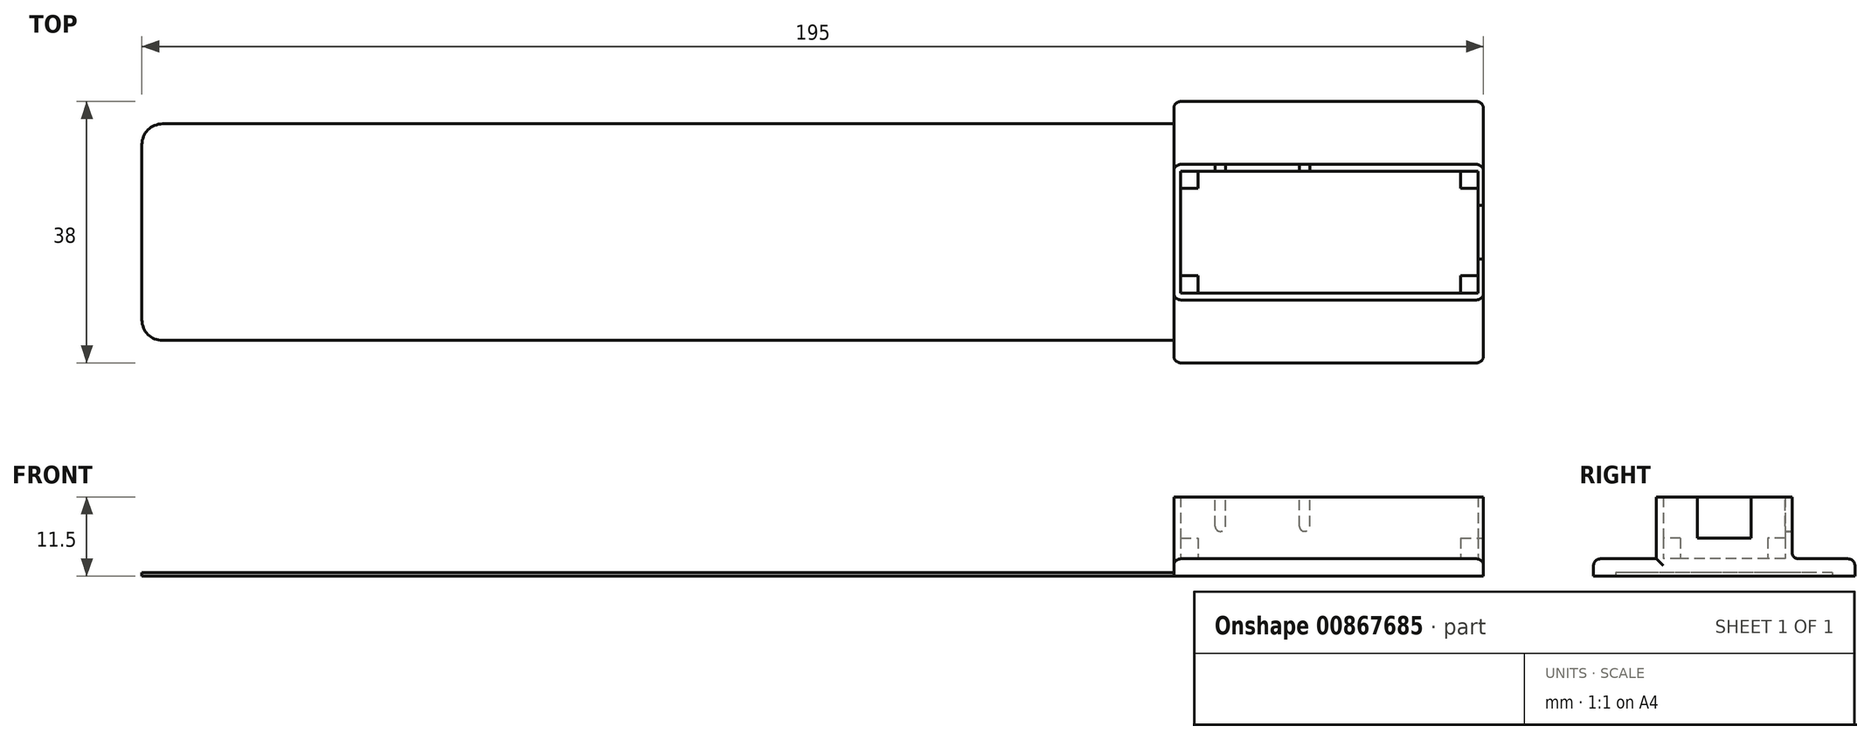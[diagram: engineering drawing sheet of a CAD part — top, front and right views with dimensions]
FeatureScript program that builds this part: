
annotation { "Feature Type Name" : "Feature", "Feature Type Description" : "" }
export const myFeature = defineFeature(function(context is Context, id is Id, definition is map)
    precondition{}
    {
        {
            var Q0;
            Q0=qCreatedBy(makeId("Top.planeOp"),FACE);
            var sketch = newSketch(context, id + "F0", { "sketchPlane" : qUnion([Q0])});
            skLineSegment(sketch, "E0.bottom", {"start": v(0, 19) * mm, "end": v(45, 19) * mm});
            skLineSegment(sketch, "E0.top", {"start": v(0, -19) * mm, "end": v(45, -19) * mm});
            skLineSegment(sketch, "E0.left", {"start": v(0, 19) * mm, "end": v(0, -19) * mm});
            skLineSegment(sketch, "E0.right", {"start": v(45, 19) * mm, "end": v(45, -19) * mm});
            skLineSegment(sketch, "E1.bottom", {"start": v(0, 15.75) * mm, "end": v(-147, 15.75) * mm});
            skLineSegment(sketch, "E1.top", {"start": v(0, -15.75) * mm, "end": v(-147, -15.75) * mm});
            skLineSegment(sketch, "E1.left", {"start": v(0, 15.75) * mm, "end": v(0, -15.75) * mm});
            skLineSegment(sketch, "E1.right", {"start": v(-150, 12.75) * mm, "end": v(-150, -12.75) * mm});
            skPoint(sketch, "E2.visualSharp", {"position": v(-150, 15.75) * mm});
            skArc(sketch, "E2.filletArc", {"start": v(-147, 15.75) * mm, "mid": v(-149.12, 14.87) * mm, "end": v(-150, 12.75) * mm});
            skPoint(sketch, "E3.visualSharp", {"position": v(-150, -15.75) * mm});
            skArc(sketch, "E3.filletArc", {"start": v(-150, -12.75) * mm, "mid": v(-149.12, -14.87) * mm, "end": v(-147, -15.75) * mm});
            skSolve(sketch);
        }
        {
            var Q0;
            Q0=makeQuery(id+"F0.imprint","IMPRINT",FACE,{"disambiguationData":[TD([[makeQuery(id+"F0.imprint","IMPRINT",EDGE,{"derivedFrom":sQuery(id+"F0.wireOp",EDGE,"E1.bottom")}),1.0]])]});
            var Q1;
            {var subQ3=sQuery(id+"F0.wireOp",EDGE,"E0.bottom");Q1=makeQuery(id+"F0.imprint","IMPRINT",FACE,{"disambiguationData":[TD([[makeQuery(id+"F0.imprint","IMPRINT",EDGE,{"derivedFrom":subQ3}),-1.0]])]});}
            extrude(context, id + "F1", {"entities" : qUnion([Q0, Q1]), "depth" : .5 * mm, "offsetDistance" : 25 * mm});
        }
        {
            var Q0;
            Q0=makeQuery(id+"F1.opExtrude","CAP_FACE",FACE,{"disambiguationData":[OSD([sQuery(id+"F0.wireOp",EDGE,"E0.bottom"),sQuery(id+"F0.wireOp",EDGE,"E0.top"),sQuery(id+"F0.wireOp",EDGE,"E0.left"),sQuery(id+"F0.wireOp",EDGE,"E0.right"),sQuery(id+"F0.wireOp",EDGE,"E1.bottom"),sQuery(id+"F0.wireOp",EDGE,"E1.top"),sQuery(id+"F0.wireOp",EDGE,"E1.right"),sQuery(id+"F0.wireOp",EDGE,"E2.filletArc"),sQuery(id+"F0.wireOp",EDGE,"E3.filletArc")])],"isStart":false});
            var sketch = newSketch(context, id + "F2", { "sketchPlane" : qUnion([Q0])});
            skLineSegment(sketch, "E4.bottom", {"start": v(45, 19) * mm, "end": v(0, 19) * mm});
            skLineSegment(sketch, "E4.top", {"start": v(45, -19) * mm, "end": v(0, -19) * mm});
            skLineSegment(sketch, "E4.left", {"start": v(45, 19) * mm, "end": v(45, -19) * mm});
            skLineSegment(sketch, "E4.right", {"start": v(0, 19) * mm, "end": v(0, -19) * mm});
            skSolve(sketch);
        }
        {
            var Q0;
            {var subQ1=sQuery(id+"F2.wireOp",EDGE,"E4.bottom");Q0=makeQuery(id+"F2.imprint","IMPRINT",FACE,{"disambiguationData":[TD([[makeQuery(id+"F2.imprint","IMPRINT",EDGE,{"derivedFrom":subQ1}),-1.0]])]});}
            extrude(context, id + "F3", {"entities" : qUnion([Q0]), "operationType" : NewBodyOperationType.ADD, "depth" : 2 * mm, "offsetDistance" : 25 * mm});
        }
        {
            var Q0;
            Q0=makeQuery(id+"F3.opExtrude","CAP_FACE",FACE,{"disambiguationData":[OSD([sQuery(id+"F2.wireOp",EDGE,"E4.bottom"),sQuery(id+"F2.wireOp",EDGE,"E4.top"),sQuery(id+"F2.wireOp",EDGE,"E4.left"),sQuery(id+"F2.wireOp",EDGE,"E4.right")])],"isStart":false});
            var sketch = newSketch(context, id + "F4", { "sketchPlane" : qUnion([Q0])});
            skLineSegment(sketch, "E5.bottom", {"start": v(1, 8.85) * mm, "end": v(44.2, 8.85) * mm});
            skLineSegment(sketch, "E5.top", {"start": v(1, -8.85) * mm, "end": v(44.2, -8.85) * mm});
            skLineSegment(sketch, "E5.left", {"start": v(1, 8.85) * mm, "end": v(1, -8.85) * mm});
            skLineSegment(sketch, "E5.right", {"start": v(44.2, 8.85) * mm, "end": v(44.2, -8.85) * mm});
            skLineSegment(sketch, "E6.bottom", {"start": v(0, 9.85) * mm, "end": v(45, 9.85) * mm});
            skLineSegment(sketch, "E6.top", {"start": v(0, -9.85) * mm, "end": v(45, -9.85) * mm});
            skLineSegment(sketch, "E6.left", {"start": v(0, 9.85) * mm, "end": v(0, -9.85) * mm});
            skLineSegment(sketch, "E6.right", {"start": v(45, 9.85) * mm, "end": v(45, -9.85) * mm});
            skSolve(sketch);
        }
        {
            var Q0;
            Q0=makeQuery(id+"F4.imprint","IMPRINT",FACE,{"disambiguationData":[TD([[makeQuery(id+"F4.imprint","IMPRINT",EDGE,{"derivedFrom":sQuery(id+"F4.wireOp",EDGE,"E5.bottom")}),1.0]])]});
            extrude(context, id + "F5", {"entities" : qUnion([Q0]), "operationType" : NewBodyOperationType.ADD, "depth" : 9 * mm, "offsetDistance" : 25 * mm});
        }
        {
            var Q0;
            Q0=makeQuery(id+"F5.boolean.opBoolean","SPLIT",FACE,{"disambiguationData":[TD([makeQuery(id+"F5.opExtrude","SWEPT_FACE",FACE,{"disambiguationData":[OSD([sQuery(id+"F4.wireOp",EDGE,"E5.bottom")])]})])],"derivedFrom":makeQuery(id+"F3.opExtrude","CAP_FACE",FACE,{"disambiguationData":[OSD([sQuery(id+"F2.wireOp",EDGE,"E4.bottom"),sQuery(id+"F2.wireOp",EDGE,"E4.top"),sQuery(id+"F2.wireOp",EDGE,"E4.left"),sQuery(id+"F2.wireOp",EDGE,"E4.right")])],"isStart":false})});
            var sketch = newSketch(context, id + "F6", { "sketchPlane" : qUnion([Q0])});
            skLineSegment(sketch, "E7.bottom", {"start": v(1, 6.35) * mm, "end": v(3.5, 6.35) * mm});
            skLineSegment(sketch, "E7.top", {"start": v(1, 8.85) * mm, "end": v(3.5, 8.85) * mm});
            skLineSegment(sketch, "E7.left", {"start": v(1, 6.35) * mm, "end": v(1, 8.85) * mm});
            skLineSegment(sketch, "E7.right", {"start": v(3.5, 6.35) * mm, "end": v(3.5, 8.85) * mm});
            skLineSegment(sketch, "E8.bottom", {"start": v(1, -6.35) * mm, "end": v(3.5, -6.35) * mm});
            skLineSegment(sketch, "E8.top", {"start": v(1, -8.85) * mm, "end": v(3.5, -8.85) * mm});
            skLineSegment(sketch, "E8.left", {"start": v(1, -6.35) * mm, "end": v(1, -8.85) * mm});
            skLineSegment(sketch, "E8.right", {"start": v(3.5, -6.35) * mm, "end": v(3.5, -8.85) * mm});
            skLineSegment(sketch, "E9.bottom", {"start": v(41.7, -8.85) * mm, "end": v(44.2, -8.85) * mm});
            skLineSegment(sketch, "E9.top", {"start": v(41.7, -6.35) * mm, "end": v(44.2, -6.35) * mm});
            skLineSegment(sketch, "E9.left", {"start": v(41.7, -8.85) * mm, "end": v(41.7, -6.35) * mm});
            skLineSegment(sketch, "E9.right", {"start": v(44.2, -8.85) * mm, "end": v(44.2, -6.35) * mm});
            skLineSegment(sketch, "E10.bottom", {"start": v(41.7, 8.85) * mm, "end": v(44.2, 8.85) * mm});
            skLineSegment(sketch, "E10.top", {"start": v(41.7, 6.35) * mm, "end": v(44.2, 6.35) * mm});
            skLineSegment(sketch, "E10.left", {"start": v(41.7, 8.85) * mm, "end": v(41.7, 6.35) * mm});
            skLineSegment(sketch, "E10.right", {"start": v(44.2, 8.85) * mm, "end": v(44.2, 6.35) * mm});
            skSolve(sketch);
        }
        {
            var Q0;
            Q0=makeQuery(id+"F6.imprint","IMPRINT",FACE,{"disambiguationData":[TD([[makeQuery(id+"F6.imprint","IMPRINT",EDGE,{"derivedFrom":sQuery(id+"F6.wireOp",EDGE,"E7.bottom")}),1.0]])]});
            var Q1;
            Q1=makeQuery(id+"F6.imprint","IMPRINT",FACE,{"disambiguationData":[TD([[makeQuery(id+"F6.imprint","IMPRINT",EDGE,{"derivedFrom":sQuery(id+"F6.wireOp",EDGE,"E10.bottom")}),-1.0]])]});
            var Q2;
            Q2=makeQuery(id+"F6.imprint","IMPRINT",FACE,{"disambiguationData":[TD([[makeQuery(id+"F6.imprint","IMPRINT",EDGE,{"derivedFrom":sQuery(id+"F6.wireOp",EDGE,"E9.bottom")}),1.0]])]});
            var Q3;
            Q3=makeQuery(id+"F6.imprint","IMPRINT",FACE,{"disambiguationData":[TD([[makeQuery(id+"F6.imprint","IMPRINT",EDGE,{"derivedFrom":sQuery(id+"F6.wireOp",EDGE,"E8.bottom")}),-1.0]])]});
            extrude(context, id + "F7", {"entities" : qUnion([Q0, Q1, Q2, Q3]), "operationType" : NewBodyOperationType.ADD, "depth" : 3 * mm, "offsetDistance" : 25 * mm});
        }
        {
            var Q0;
            Q0=makeQuery(id+"F5.boolean.opBoolean","MERGE",FACE,{"derivedFrom":[makeQuery(id+"F3.boolean.opBoolean","MERGE",FACE,{"derivedFrom":[makeQuery(id+"F1.opExtrude","SWEPT_FACE",FACE,{"disambiguationData":[OSD([sQuery(id+"F0.wireOp",EDGE,"E0.right")])]}),makeQuery(id+"F3.opExtrude","SWEPT_FACE",FACE,{"disambiguationData":[OSD([sQuery(id+"F2.wireOp",EDGE,"E4.left")])]})]}),makeQuery(id+"F5.opExtrude","SWEPT_FACE",FACE,{"disambiguationData":[OSD([sQuery(id+"F4.wireOp",EDGE,"E6.right")])]})]});
            var sketch = newSketch(context, id + "F8", { "sketchPlane" : qUnion([Q0])});
            skLineSegment(sketch, "E11.bottom", {"start": v(-3.9, 11.5) * mm, "end": v(3.9, 11.5) * mm});
            skLineSegment(sketch, "E11.top", {"start": v(-3.9, 5.5) * mm, "end": v(3.9, 5.5) * mm});
            skLineSegment(sketch, "E11.left", {"start": v(-3.9, 11.5) * mm, "end": v(-3.9, 5.5) * mm});
            skLineSegment(sketch, "E11.right", {"start": v(3.9, 11.5) * mm, "end": v(3.9, 5.5) * mm});
            skSolve(sketch);
        }
        {
            var Q0;
            Q0=makeQuery(id+"F8.imprint","IMPRINT",FACE,{"disambiguationData":[TD([[makeQuery(id+"F8.imprint","IMPRINT",EDGE,{"derivedFrom":sQuery(id+"F8.wireOp",EDGE,"E11.bottom")}),1.0]])]});
            extrude(context, id + "F9", {"entities" : qUnion([Q0]), "operationType" : NewBodyOperationType.REMOVE, "endBound" : BoundingType.UP_TO_NEXT, "oppositeDirection" : true, "depth" : 25 * mm, "offsetDistance" : 25 * mm});
        }
        {
            var Q0;
            Q0=makeQuery(id+"F5.opExtrude","SWEPT_FACE",FACE,{"disambiguationData":[OSD([sQuery(id+"F4.wireOp",EDGE,"E6.bottom")])]});
            var sketch = newSketch(context, id + "F10", { "sketchPlane" : qUnion([Q0])});
            skLineSegment(sketch, "E12.bottom", {"start": v(-19.75, 11.5) * mm, "end": v(-18.25, 11.5) * mm});
            skLineSegment(sketch, "E12.top", {"start": v(-19.75, 6.5) * mm, "end": v(-18.25, 6.5) * mm});
            skLineSegment(sketch, "E12.left", {"start": v(-19.75, 11.5) * mm, "end": v(-19.75, 6.5) * mm});
            skLineSegment(sketch, "E12.right", {"start": v(-18.25, 11.5) * mm, "end": v(-18.25, 6.5) * mm});
            skLineSegment(sketch, "E13.bottom", {"start": v(-7.5, 11.5) * mm, "end": v(-6, 11.5) * mm});
            skLineSegment(sketch, "E13.top", {"start": v(-7.5, 6.5) * mm, "end": v(-6, 6.5) * mm});
            skLineSegment(sketch, "E13.left", {"start": v(-7.5, 11.5) * mm, "end": v(-7.5, 6.5) * mm});
            skLineSegment(sketch, "E13.right", {"start": v(-6, 11.5) * mm, "end": v(-6, 6.5) * mm});
            skSolve(sketch);
        }
        {
            var Q0;
            Q0=makeQuery(id+"F10.imprint","IMPRINT",FACE,{"disambiguationData":[TD([[makeQuery(id+"F10.imprint","IMPRINT",EDGE,{"derivedFrom":sQuery(id+"F10.wireOp",EDGE,"E12.bottom")}),1.0]])]});
            var Q1;
            Q1=makeQuery(id+"F10.imprint","IMPRINT",FACE,{"disambiguationData":[TD([[makeQuery(id+"F10.imprint","IMPRINT",EDGE,{"derivedFrom":sQuery(id+"F10.wireOp",EDGE,"E13.bottom")}),1.0]])]});
            extrude(context, id + "F11", {"entities" : qUnion([Q0, Q1]), "operationType" : NewBodyOperationType.REMOVE, "endBound" : BoundingType.UP_TO_NEXT, "oppositeDirection" : true, "depth" : 25 * mm, "offsetDistance" : 25 * mm});
        }
        {
            var Q0;
            Q0=makeQuery(id+"F11.boolean.opBoolean","COPY",EDGE,{"derivedFrom":makeQuery(id+"F11.opExtrude","SWEPT_EDGE",EDGE,{"disambiguationData":[OSD([sQuery(id+"F10.wireOp",EDGE,"E12.top"),sQuery(id+"F10.wireOp",EDGE,"E12.right")])]})});
            var Q1;
            Q1=makeQuery(id+"F11.boolean.opBoolean","COPY",EDGE,{"derivedFrom":makeQuery(id+"F11.opExtrude","SWEPT_EDGE",EDGE,{"disambiguationData":[OSD([sQuery(id+"F10.wireOp",EDGE,"E12.top"),sQuery(id+"F10.wireOp",EDGE,"E12.left")])]})});
            var Q2;
            Q2=makeQuery(id+"F11.boolean.opBoolean","COPY",EDGE,{"derivedFrom":makeQuery(id+"F11.opExtrude","SWEPT_EDGE",EDGE,{"disambiguationData":[OSD([sQuery(id+"F10.wireOp",EDGE,"E13.top"),sQuery(id+"F10.wireOp",EDGE,"E13.right")])]})});
            var Q3;
            Q3=makeQuery(id+"F11.boolean.opBoolean","COPY",EDGE,{"derivedFrom":makeQuery(id+"F11.opExtrude","SWEPT_EDGE",EDGE,{"disambiguationData":[OSD([sQuery(id+"F10.wireOp",EDGE,"E13.top"),sQuery(id+"F10.wireOp",EDGE,"E13.left")])]})});
            fillet(context, id + "F12", {"entities" : qUnion([Q0, Q1, Q2, Q3]), "radius" : .75 * mm, "tangentPropagation" : true, "allowEdgeOverflow" : false});
        }
        {
            var Q0;
            Q0=makeQuery(id+"F5.opExtrude","SWEPT_EDGE",EDGE,{"disambiguationData":[OSD([sQuery(id+"F2.wireOp",EDGE,"E4.left"),sQuery(id+"F4.wireOp",EDGE,"E6.bottom"),sQuery(id+"F4.wireOp",EDGE,"E6.right")])]});
            var Q1;
            {var subQ1=sQuery(id+"F2.wireOp",EDGE,"E4.left");Q1=makeQuery(id+"F5.boolean.opBoolean","SPLIT",EDGE,{"disambiguationData":[TD([makeQuery(id+"F1.opExtrude","SWEPT_FACE",FACE,{"disambiguationData":[OSD([sQuery(id+"F0.wireOp",EDGE,"E0.bottom")])]})])],"derivedFrom":makeQuery(id+"F3.opExtrude","CAP_EDGE",EDGE,{"disambiguationData":[OSD([subQ1])],"isStart":false})});}
            var Q2;
            Q2=makeQuery(id+"F3.boolean.opBoolean","MERGE",EDGE,{"derivedFrom":[makeQuery(id+"F1.opExtrude","SWEPT_EDGE",EDGE,{"disambiguationData":[OSD([sQuery(id+"F0.wireOp",EDGE,"E0.bottom"),sQuery(id+"F0.wireOp",EDGE,"E0.right")])]}),makeQuery(id+"F3.opExtrude","SWEPT_EDGE",EDGE,{"disambiguationData":[OSD([sQuery(id+"F2.wireOp",EDGE,"E4.bottom"),sQuery(id+"F2.wireOp",EDGE,"E4.left")])]})]});
            var Q3;
            Q3=makeQuery(id+"F3.opExtrude","CAP_EDGE",EDGE,{"disambiguationData":[OSD([sQuery(id+"F2.wireOp",EDGE,"E4.bottom")])],"isStart":false});
            var Q4;
            {var subQ2=sQuery(id+"F0.wireOp",EDGE,"E0.bottom");var subQ4=sQuery(id+"F2.wireOp",EDGE,"E4.right");Q4=makeQuery(id+"F5.boolean.opBoolean","SPLIT",EDGE,{"disambiguationData":[TD([makeQuery(id+"F1.opExtrude","SWEPT_FACE",FACE,{"disambiguationData":[OSD([subQ2])]})])],"derivedFrom":makeQuery(id+"F3.opExtrude","CAP_EDGE",EDGE,{"disambiguationData":[OSD([subQ4])],"isStart":false})});}
            var Q5;
            Q5=makeQuery(id+"F5.opExtrude","SWEPT_EDGE",EDGE,{"disambiguationData":[OSD([sQuery(id+"F2.wireOp",EDGE,"E4.right"),sQuery(id+"F4.wireOp",EDGE,"E6.bottom"),sQuery(id+"F4.wireOp",EDGE,"E6.left")])]});
            var Q6;
            Q6=makeQuery(id+"F5.opExtrude","CAP_EDGE",EDGE,{"disambiguationData":[OSD([sQuery(id+"F4.wireOp",EDGE,"E6.bottom")])],"isStart":true});
            var Q7;
            Q7=makeQuery(id+"F5.opExtrude","SWEPT_EDGE",EDGE,{"disambiguationData":[OSD([sQuery(id+"F2.wireOp",EDGE,"E4.right"),sQuery(id+"F4.wireOp",EDGE,"E6.top"),sQuery(id+"F4.wireOp",EDGE,"E6.left")])]});
            var Q8;
            {var subQ0=sQuery(id+"F2.wireOp",EDGE,"E4.right");var subQ2=sQuery(id+"F0.wireOp",EDGE,"E0.top");Q8=makeQuery(id+"F5.boolean.opBoolean","SPLIT",EDGE,{"disambiguationData":[TD([makeQuery(id+"F1.opExtrude","SWEPT_FACE",FACE,{"disambiguationData":[OSD([subQ2])]})])],"derivedFrom":makeQuery(id+"F3.opExtrude","CAP_EDGE",EDGE,{"disambiguationData":[OSD([subQ0])],"isStart":false})});}
            var Q9;
            Q9=makeQuery(id+"F3.boolean.opBoolean","MERGE",EDGE,{"derivedFrom":[makeQuery(id+"F1.opExtrude","SWEPT_EDGE",EDGE,{"disambiguationData":[OSD([sQuery(id+"F0.wireOp",EDGE,"E0.top"),sQuery(id+"F0.wireOp",EDGE,"E0.left")])]}),makeQuery(id+"F3.opExtrude","SWEPT_EDGE",EDGE,{"disambiguationData":[OSD([sQuery(id+"F2.wireOp",EDGE,"E4.top"),sQuery(id+"F2.wireOp",EDGE,"E4.right")])]})]});
            var Q10;
            Q10=makeQuery(id+"F3.opExtrude","CAP_EDGE",EDGE,{"disambiguationData":[OSD([sQuery(id+"F2.wireOp",EDGE,"E4.top")])],"isStart":false});
            var Q11;
            Q11=makeQuery(id+"F5.opExtrude","CAP_EDGE",EDGE,{"disambiguationData":[OSD([sQuery(id+"F4.wireOp",EDGE,"E6.top")])],"isStart":true});
            var Q12;
            Q12=makeQuery(id+"F5.opExtrude","SWEPT_EDGE",EDGE,{"disambiguationData":[OSD([sQuery(id+"F2.wireOp",EDGE,"E4.left"),sQuery(id+"F4.wireOp",EDGE,"E6.top"),sQuery(id+"F4.wireOp",EDGE,"E6.right")])]});
            var Q13;
            {var subQ0=sQuery(id+"F2.wireOp",EDGE,"E4.left");Q13=makeQuery(id+"F5.boolean.opBoolean","SPLIT",EDGE,{"disambiguationData":[TD([makeQuery(id+"F1.opExtrude","SWEPT_FACE",FACE,{"disambiguationData":[OSD([sQuery(id+"F0.wireOp",EDGE,"E0.top")])]})])],"derivedFrom":makeQuery(id+"F3.opExtrude","CAP_EDGE",EDGE,{"disambiguationData":[OSD([subQ0])],"isStart":false})});}
            var Q14;
            Q14=makeQuery(id+"F3.boolean.opBoolean","MERGE",EDGE,{"derivedFrom":[makeQuery(id+"F1.opExtrude","SWEPT_EDGE",EDGE,{"disambiguationData":[OSD([sQuery(id+"F0.wireOp",EDGE,"E0.top"),sQuery(id+"F0.wireOp",EDGE,"E0.right")])]}),makeQuery(id+"F3.opExtrude","SWEPT_EDGE",EDGE,{"disambiguationData":[OSD([sQuery(id+"F2.wireOp",EDGE,"E4.top"),sQuery(id+"F2.wireOp",EDGE,"E4.left")])]})]});
            var Q15;
            Q15=makeQuery(id+"F3.boolean.opBoolean","MERGE",EDGE,{"derivedFrom":[makeQuery(id+"F1.opExtrude","SWEPT_EDGE",EDGE,{"disambiguationData":[OSD([sQuery(id+"F0.wireOp",EDGE,"E0.bottom"),sQuery(id+"F0.wireOp",EDGE,"E0.left")])]}),makeQuery(id+"F3.opExtrude","SWEPT_EDGE",EDGE,{"disambiguationData":[OSD([sQuery(id+"F2.wireOp",EDGE,"E4.bottom"),sQuery(id+"F2.wireOp",EDGE,"E4.right")])]})]});
            fillet(context, id + "F13", {"entities" : qUnion([Q0, Q1, Q2, Q3, Q4, Q5, Q6, Q7, Q8, Q9, Q10, Q11, Q12, Q13, Q14, Q15]), "radius" : 1 * mm, "tangentPropagation" : true, "allowEdgeOverflow" : false});
        }
    });
